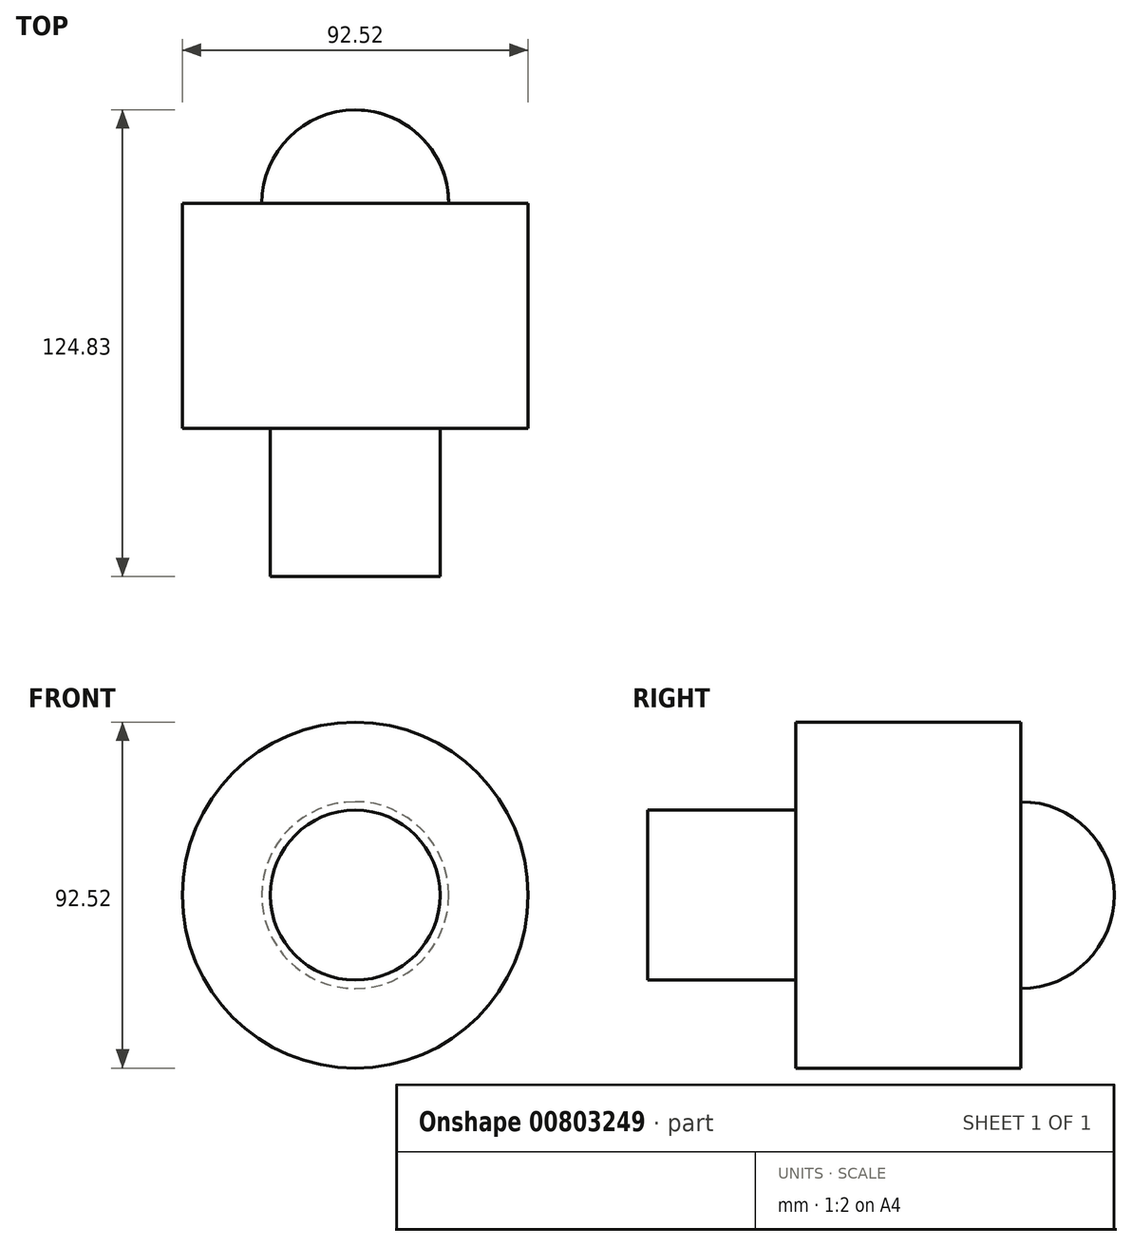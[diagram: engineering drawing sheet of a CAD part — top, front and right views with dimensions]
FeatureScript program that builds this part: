
annotation { "Feature Type Name" : "Feature", "Feature Type Description" : "" }
export const myFeature = defineFeature(function(context is Context, id is Id, definition is map)
    precondition{}
    {
        {
            var Q0;
            Q0=qCreatedBy(makeId("Top.planeOp"),FACE);
            var sketch = newSketch(context, id + "F0", { "sketchPlane" : qUnion([Q0])});
            skLineSegment(sketch, "E0", {"start": v(0, 75.17) * mm, "end": v(0, -74.83) * mm, "construction": true});
            skLineSegment(sketch, "E1.bottom", {"start": v(25, 44.9) * mm, "end": v(46.26, 44.9) * mm});
            skLineSegment(sketch, "E1.top", {"start": v(22.72, -15.33) * mm, "end": v(46.26, -15.33) * mm});
            skLineSegment(sketch, "E1.left", {"start": v(0, 44.9) * mm, "end": v(0, -15.33) * mm});
            skLineSegment(sketch, "E1.right", {"start": v(46.26, 44.9) * mm, "end": v(46.26, -15.33) * mm});
            skLineSegment(sketch, "E2.top", {"start": v(22.72, -54.93) * mm, "end": v(0, -54.93) * mm});
            skLineSegment(sketch, "E2.left", {"start": v(22.72, -15.33) * mm, "end": v(22.72, -54.93) * mm});
            skArc(sketch, "E3", {"start": v(25, 44.9) * mm, "mid": v(17.68, 62.57) * mm, "end": v(0, 69.9) * mm});
            skPoint(sketch, "E4.orphan", {"position": v(22.72, 0) * mm});
            skLineSegment(sketch, "E5", {"start": v(0, 69.9) * mm, "end": v(0, -54.93) * mm});
            skSolve(sketch);
        }
        {
            var Q0;
            Q0=makeQuery(id+"F0.imprint","IMPRINT",FACE,{"disambiguationData":[TD([[makeQuery(id+"F0.imprint","IMPRINT",EDGE,{"derivedFrom":sQuery(id+"F0.wireOp",EDGE,"E1.bottom")}),-1.0]])]});
            var Q1;
            Q1=sQuery(id+"F0.wireOp",EDGE,"E0");
            revolve(context, id + "F1", {"surfaceOperationType" : NewSurfaceOperationType.NEW, "entities" : qUnion([Q0]), "axis" : qUnion([Q1]), "revolveType" : RevolveType.FULL});
        }
    });
